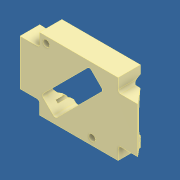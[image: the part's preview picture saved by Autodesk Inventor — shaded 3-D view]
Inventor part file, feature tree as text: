
AUTODESK INVENTOR PART (.ipt)
format: ipt  version: 2018 (Build 220112000, 112)  size: 241,152 bytes
history: native  units: mm
features: extrude x7, sketch x7, fillet x2, plane x1
ambient origin geometry x8: Origin, YZ Plane, XZ Plane, XY Plane, X Axis, Y Axis, Z Axis, Center Point
bodies: Body1 (feature_tree)
feature tree (17):
  extrude  "Extrusion21"  Depth=55.0mm
  extrude  "Extrusion22"  Depth=17.0mm TaperAngle=0.0deg
  extrude  "Extrusion23"  Depth=5.0mm
  plane  "Work Plane2"
  extrude  "Extrusion24"  Depth=5.0mm
  extrude  "Extrusion25"  Depth=55.0mm
  fillet  "Fillet4"  Radius=14.0mm
  extrude  "Extrusion27"  Depth=16.311923mm
  fillet  "Fillet5"  [1 undecoded]
  extrude  "Extrusion28"  Depth=2.0mm TaperAngle=0.0deg
  sketch  "Sketch24"  dims[d41=2.9mm d160=55.0mm]
  sketch  "Sketch25"  dims[d161=90.0mm d162=17.0mm d163=0.0mm]
  sketch  "Sketch29"  dims[d168=20.0mm d169=55.0mm d170=14.0mm d171=0.0mm]
  sketch  "Sketch31"  dims[d172=15.0mm d173=52.0mm d176=47.376154mm d177=47.376154mm d181=16.311923mm d182=45.0deg]
  sketch  "Sketch32"  dims[d183=3.811923mm d184=15.0mm d185=0.0mm d187=45.0mm d192=29.0mm d194=27.0mm d195=15.0mm d196=0.0mm d213=10.5mm d214=0.0mm d216=2.2mm d217=1.1mm d218=3.3mm d219=2.4mm d220=2.0mm d221=7.5mm d222=15.0mm d227=15.0mm d228=10.0mm d229=45.0mm d230=90.0mm d231=10.5mm d232=0.0mm d233=2.0mm d234=8.726646mm d235=10.5mm d236=0.0mm d237=-0.349066mm]
  sketch  "Sketch26"  dims[d164=5.0mm d165=5.0mm]
  sketch  "Sketch28"  dims[d166=5.0mm d167=5.0mm]
note: 1 required parameter value undecoded (feature->parameter linkage not recoverable at this tier; creation-order binding heuristic only, values carry confidence <= 0.55)
